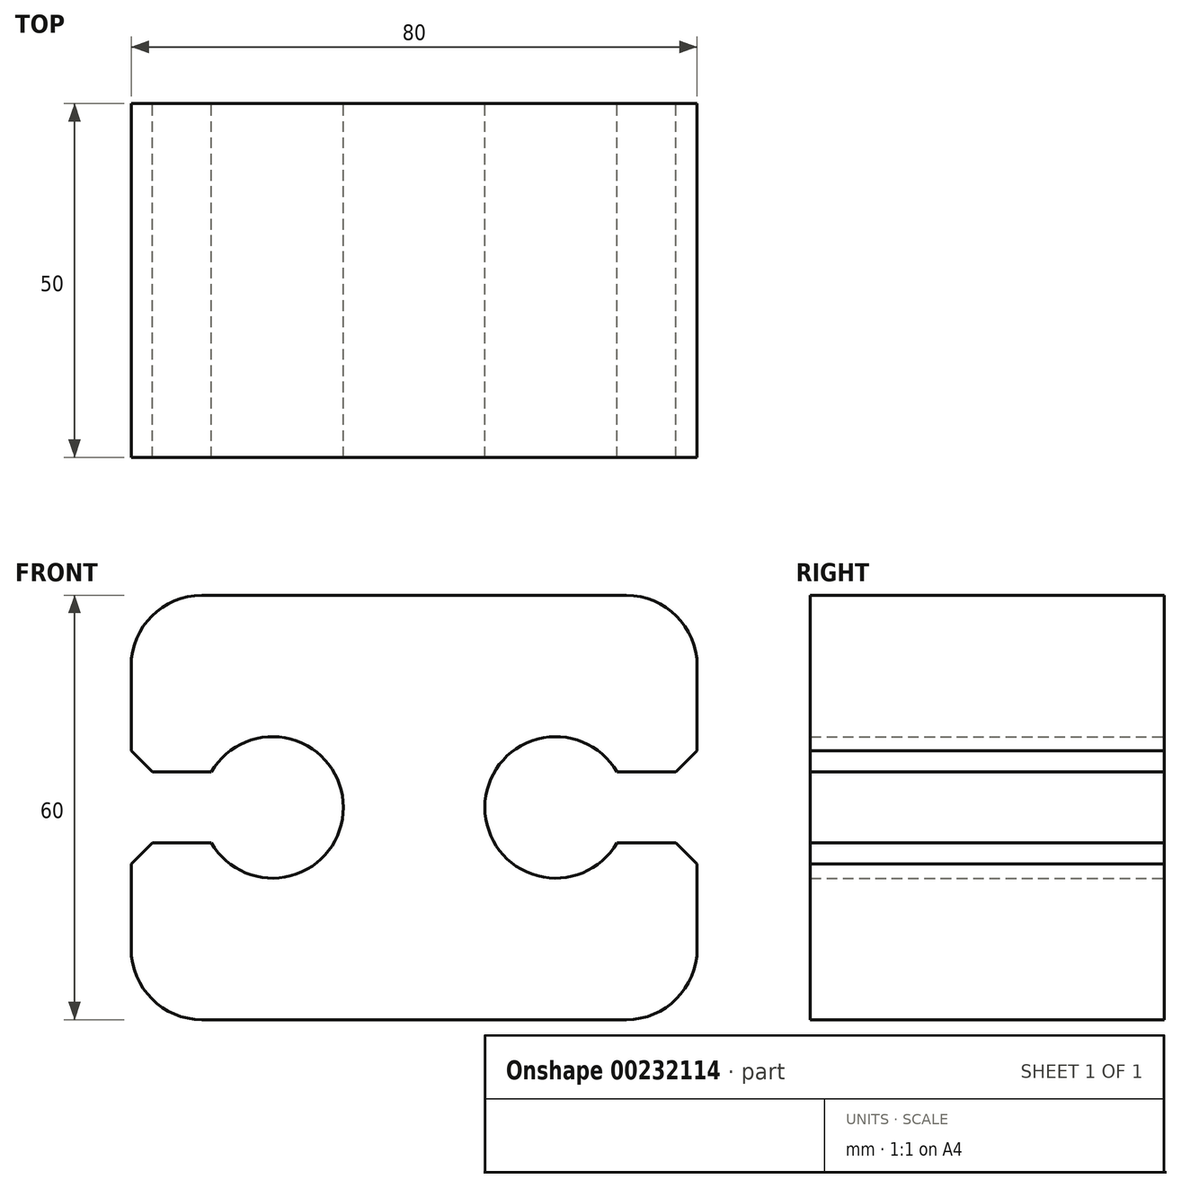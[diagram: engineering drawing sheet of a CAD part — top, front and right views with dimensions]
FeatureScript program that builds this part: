
annotation { "Feature Type Name" : "Feature", "Feature Type Description" : "" }
export const myFeature = defineFeature(function(context is Context, id is Id, definition is map)
    precondition{}
    {
        {
            var Q0;
            Q0=qCreatedBy(makeId("Front.planeOp"),FACE);
            var sketch = newSketch(context, id + "F0", { "sketchPlane" : qUnion([Q0])});
            skLineSegment(sketch, "E0", {"start": v(0, 0) * mm, "end": v(0, 94.44) * mm, "construction": true});
            skLineSegment(sketch, "E1.bottom", {"start": v(0, 0) * mm, "end": v(-30, 0) * mm});
            skLineSegment(sketch, "E1.top", {"start": v(0, 60) * mm, "end": v(-30, 60) * mm});
            skLineSegment(sketch, "E1.right", {"start": v(-40, 10) * mm, "end": v(-40, 22) * mm});
            skPoint(sketch, "E2.visualSharp", {"position": v(-40, 60) * mm});
            skArc(sketch, "E2.filletArc", {"start": v(-30, 60) * mm, "mid": v(-37.07, 57.07) * mm, "end": v(-40, 50) * mm});
            skPoint(sketch, "E3.visualSharp", {"position": v(-40, 0) * mm});
            skArc(sketch, "E3.filletArc", {"start": v(-40, 10) * mm, "mid": v(-37.07, 2.93) * mm, "end": v(-30, 0) * mm});
            skPoint(sketch, "E4", {"position": v(-40, 30) * mm});
            skArc(sketch, "E5", {"start": v(-28.66, 25) * mm, "mid": v(-10, 30) * mm, "end": v(-28.66, 35) * mm});
            skLineSegment(sketch, "E6", {"start": v(-28.66, 35) * mm, "end": v(-37, 35) * mm});
            skLineSegment(sketch, "E7", {"start": v(-40, 30) * mm, "end": v(101.28, 30) * mm, "construction": true});
            skLineSegment(sketch, "E8.MirrorCS", {"start": v(-28.66, 25) * mm, "end": v(-37, 25) * mm});
            skLineSegment(sketch, "E9", {"start": v(-40, 38) * mm, "end": v(-37, 35) * mm});
            skLineSegment(sketch, "E10.trimOffspring", {"start": v(-40, 38) * mm, "end": v(-40, 50) * mm});
            skPoint(sketch, "E11.orphan", {"position": v(-40, 35) * mm});
            skLineSegment(sketch, "E12.MirrorCS", {"start": v(-40, 22) * mm, "end": v(-37, 25) * mm});
            skPoint(sketch, "E13.orphan", {"position": v(-40, 25) * mm});
            skLineSegment(sketch, "E14.MirrorCS", {"start": v(40, 38) * mm, "end": v(37, 35) * mm});
            skLineSegment(sketch, "E15.MirrorCS", {"start": v(40, 30) * mm, "end": v(-101.28, 30) * mm, "construction": true});
            skPoint(sketch, "E16.MirrorP", {"position": v(40, 30) * mm});
            skLineSegment(sketch, "E17.MirrorCS", {"start": v(0, 0) * mm, "end": v(30, 0) * mm});
            skPoint(sketch, "E18.MirrorP", {"position": v(40, 60) * mm});
            skPoint(sketch, "E19.MirrorP", {"position": v(40, 25) * mm});
            skLineSegment(sketch, "E20.MirrorCS", {"start": v(40, 10) * mm, "end": v(40, 22) * mm});
            skArc(sketch, "E21.MirrorCS", {"start": v(28.66, 25) * mm, "mid": v(10, 30) * mm, "end": v(28.66, 35) * mm});
            skPoint(sketch, "E22.MirrorP", {"position": v(40, 35) * mm});
            skLineSegment(sketch, "E23.MirrorCS", {"start": v(28.66, 35) * mm, "end": v(37, 35) * mm});
            skLineSegment(sketch, "E24.MirrorCS", {"start": v(28.66, 25) * mm, "end": v(37, 25) * mm});
            skLineSegment(sketch, "E25.MirrorCS", {"start": v(40, 38) * mm, "end": v(40, 50) * mm});
            skLineSegment(sketch, "E26.MirrorCS", {"start": v(40, 22) * mm, "end": v(37, 25) * mm});
            skLineSegment(sketch, "E27.MirrorCS", {"start": v(0, 60) * mm, "end": v(30, 60) * mm});
            skPoint(sketch, "E28.MirrorP", {"position": v(40, 0) * mm});
            skArc(sketch, "E29.MirrorCS", {"start": v(30, 60) * mm, "mid": v(37.07, 57.07) * mm, "end": v(40, 50) * mm});
            skArc(sketch, "E30.MirrorCS", {"start": v(40, 10) * mm, "mid": v(37.07, 2.93) * mm, "end": v(30, 0) * mm});
            skSolve(sketch);
        }
        {
            var Q0;
            Q0=makeQuery(id+"F0.imprint","IMPRINT",FACE,{"disambiguationData":[TD([[makeQuery(id+"F0.imprint","IMPRINT",EDGE,{"derivedFrom":sQuery(id+"F0.wireOp",EDGE,"E1.bottom")}),-1.0]])]});
            extrude(context, id + "F1", {"entities" : qUnion([Q0]), "depth" : 50 * mm});
        }
    });
